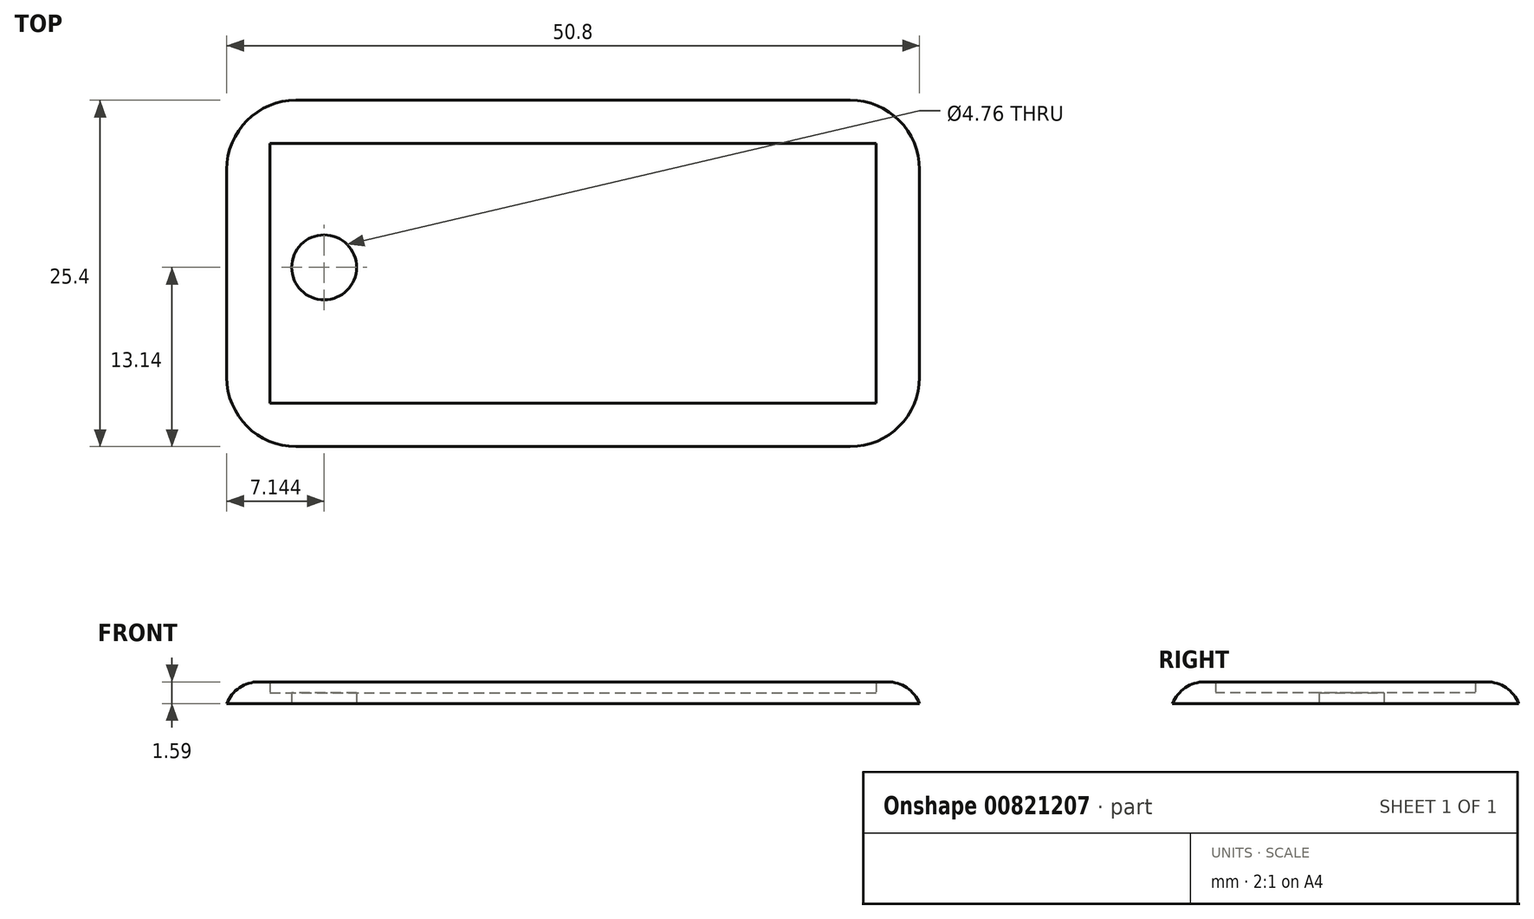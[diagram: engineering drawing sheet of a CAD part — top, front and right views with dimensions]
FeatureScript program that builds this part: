
annotation { "Feature Type Name" : "Feature", "Feature Type Description" : "" }
export const myFeature = defineFeature(function(context is Context, id is Id, definition is map)
    precondition{}
    {
        {
            var Q0;
            Q0=qCreatedBy(makeId("Top.planeOp"),FACE);
            var sketch = newSketch(context, id + "F0", { "sketchPlane" : qUnion([Q0])});
            skLineSegment(sketch, "E0.bottom", {"start": v(0, 25.4) * mm, "end": v(50.8, 25.4) * mm});
            skLineSegment(sketch, "E0.top", {"start": v(0, 0) * mm, "end": v(50.8, 0) * mm});
            skLineSegment(sketch, "E0.left", {"start": v(0, 25.4) * mm, "end": v(0, 0) * mm});
            skLineSegment(sketch, "E0.right", {"start": v(50.8, 25.4) * mm, "end": v(50.8, 0) * mm});
            skCircle(sketch, "E1", {"center": v(7.14, 13.14) * mm, "radius": 2.38 * mm});
            skLineSegment(sketch, "E2.bottom", {"start": v(3.18, 22.22) * mm, "end": v(47.63, 22.22) * mm});
            skLineSegment(sketch, "E2.top", {"start": v(3.18, 3.17) * mm, "end": v(47.63, 3.17) * mm});
            skLineSegment(sketch, "E2.left", {"start": v(3.18, 22.22) * mm, "end": v(3.18, 3.17) * mm});
            skLineSegment(sketch, "E2.right", {"start": v(47.63, 22.22) * mm, "end": v(47.63, 3.17) * mm});
            skSolve(sketch);
        }
        {
            var Q0;
            Q0=makeQuery(id+"F0.imprint","IMPRINT",FACE,{"disambiguationData":[TD([[makeQuery(id+"F0.imprint","IMPRINT",EDGE,{"derivedFrom":sQuery(id+"F0.wireOp",EDGE,"E1")}),-1.0]])]});
            extrude(context, id + "F1", {"entities" : qUnion([Q0]), "depth" : 0.8 * mm, "offsetDistance" : 25.4 * mm});
        }
        {
            var Q0;
            Q0 = qSketchRegion(id + "F0", true);
            extrude(context, id + "F2", {"entities" : qUnion([Q0]), "operationType" : NewBodyOperationType.ADD, "depth" : 1.59 * mm, "offsetDistance" : 25.4 * mm});
        }
        {
            var Q0;
            Q0=makeQuery(id+"F2.opExtrude","SWEPT_EDGE",EDGE,{"disambiguationData":[OSD([sQuery(id+"F0.wireOp",EDGE,"E0.top"),sQuery(id+"F0.wireOp",EDGE,"E0.right")])]});
            var Q1;
            Q1=makeQuery(id+"F2.opExtrude","SWEPT_EDGE",EDGE,{"disambiguationData":[OSD([sQuery(id+"F0.wireOp",EDGE,"E0.bottom"),sQuery(id+"F0.wireOp",EDGE,"E0.right")])]});
            var Q2;
            Q2=makeQuery(id+"F2.opExtrude","SWEPT_EDGE",EDGE,{"disambiguationData":[OSD([sQuery(id+"F0.wireOp",EDGE,"E0.top"),sQuery(id+"F0.wireOp",EDGE,"E0.left")])]});
            var Q3;
            Q3=makeQuery(id+"F2.opExtrude","SWEPT_EDGE",EDGE,{"disambiguationData":[OSD([sQuery(id+"F0.wireOp",EDGE,"E0.bottom"),sQuery(id+"F0.wireOp",EDGE,"E0.left")])]});
            fillet(context, id + "F3", {"entities" : qUnion([Q0, Q1, Q2, Q3]), "radius" : 5.08 * mm, "tangentPropagation" : true, "allowEdgeOverflow" : false});
        }
        {
            var Q0;
            Q0=makeQuery(id+"F2.opExtrude","CAP_EDGE",EDGE,{"disambiguationData":[OSD([sQuery(id+"F0.wireOp",EDGE,"E0.top")])],"isStart":false});
            fillet(context, id + "F4", {"entities" : qUnion([Q0]), "radius" : 2.54 * mm, "tangentPropagation" : true, "allowEdgeOverflow" : false});
        }
        {
            var Q0;
            Q0=qCreatedBy(makeId("Top.planeOp"),FACE);
            var sketch = newSketch(context, id + "F5", { "sketchPlane" : qUnion([Q0])});
            skText(sketch, "E3", { "text": "Joe", "fontName": "OpenSans-BoldItalic.ttf"});
            const initialGuessF5  = {"E3": [0.01139, 0.00594, 1, 0, 0.01343]};
            skSetInitialGuess(sketch, initialGuessF5);
            skSolve(sketch);
        }
        {
            var Q0;
            Q0 = qSketchRegion(id + "F5", true);
            extrude(context, id + "F6", {"entities" : qUnion([Q0]), "operationType" : NewBodyOperationType.ADD, "depth" : 1 / 812.8 * mm, "offsetDistance" : 25.4 * mm});
        }
    });
